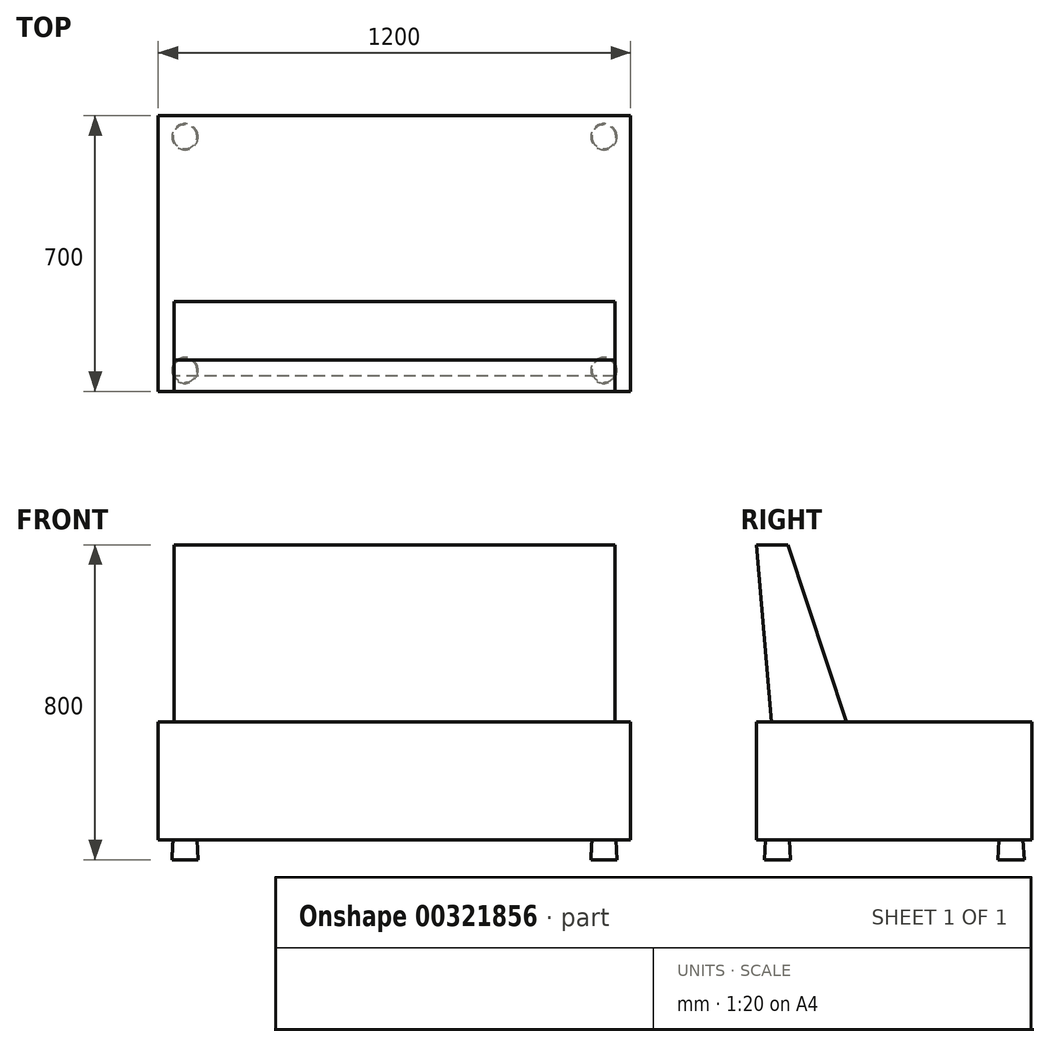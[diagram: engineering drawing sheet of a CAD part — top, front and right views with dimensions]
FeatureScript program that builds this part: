
annotation { "Feature Type Name" : "Feature", "Feature Type Description" : "" }
export const myFeature = defineFeature(function(context is Context, id is Id, definition is map)
    precondition{}
    {
        {
            var Q0;
            Q0=qCreatedBy(makeId("Top.planeOp"),FACE);
            var sketch = newSketch(context, id + "F0", { "sketchPlane" : qUnion([Q0])});
            skLineSegment(sketch, "E0.bottom", {"start": v(600, -350) * mm, "end": v(-600, -350) * mm});
            skLineSegment(sketch, "E0.top", {"start": v(600, 350) * mm, "end": v(-600, 350) * mm});
            skLineSegment(sketch, "E0.left", {"start": v(600, -350) * mm, "end": v(600, 350) * mm});
            skLineSegment(sketch, "E0.right", {"start": v(-600, -350) * mm, "end": v(-600, 350) * mm});
            skPoint(sketch, "E0.middle", {"position": v(0, 0) * mm});
            skSolve(sketch);
        }
        {
            var Q0;
            Q0=makeQuery(id+"F0.imprint","IMPRINT",FACE,{"disambiguationData":[TD([[makeQuery(id+"F0.imprint","IMPRINT",EDGE,{"derivedFrom":sQuery(id+"F0.wireOp",EDGE,"E0.bottom")}),-1.0]])]});
            extrude(context, id + "F1", {"entities" : qUnion([Q0]), "depth" : 300 * mm});
        }
        {
            var Q0;
            Q0=makeQuery(id+"F1.opExtrude","CAP_FACE",FACE,{"disambiguationData":[OSD([sQuery(id+"F0.wireOp",EDGE,"E0.bottom"),sQuery(id+"F0.wireOp",EDGE,"E0.top"),sQuery(id+"F0.wireOp",EDGE,"E0.left"),sQuery(id+"F0.wireOp",EDGE,"E0.right")])],"isStart":true});
            var sketch = newSketch(context, id + "F2", { "sketchPlane" : qUnion([Q0])});
            skLineSegment(sketch, "E1", {"start": v(-600, 0) * mm, "end": v(600, 0) * mm, "construction": true});
            skLineSegment(sketch, "E2", {"start": v(0, -350) * mm, "end": v(0, 350) * mm, "construction": true});
            skCircle(sketch, "E3", {"center": v(-532.1, -296.66) * mm, "radius": 30.5 * mm});
            skCircle(sketch, "E4.MirrorC", {"center": v(532.1, -296.66) * mm, "radius": 30.5 * mm});
            skCircle(sketch, "E5.MirrorC", {"center": v(532.1, 296.66) * mm, "radius": 30.5 * mm});
            skCircle(sketch, "E6.MirrorC", {"center": v(-532.1, 296.66) * mm, "radius": 30.5 * mm});
            skSolve(sketch);
        }
        {
            var Q0;
            Q0 = qSketchRegion(id + "F2", true);
            extrude(context, id + "F3", {"entities" : qUnion([Q0]), "operationType" : NewBodyOperationType.ADD, "depth" : 50 * mm, "hasDraft" : true, "draftAngle" : 3 * degree});
        }
        {
            var Q0;
            Q0=qCreatedBy(makeId("Right.planeOp"),FACE);
            var sketch = newSketch(context, id + "F4", { "sketchPlane" : qUnion([Q0])});
            skLineSegment(sketch, "E7", {"start": v(-107, 254.91) * mm, "end": v(-270.1, 750) * mm});
            skLineSegment(sketch, "E8", {"start": v(-270.1, 750) * mm, "end": v(-350, 750) * mm});
            skLineSegment(sketch, "E9", {"start": v(-350, 750) * mm, "end": v(-305.83, 230.6) * mm});
            skLineSegment(sketch, "E10", {"start": v(-305.83, 230.6) * mm, "end": v(-107, 254.91) * mm});
            skSolve(sketch);
        }
        {
            var Q0;
            Q0 = qSketchRegion(id + "F4", true);
            extrude(context, id + "F5", {"entities" : qUnion([Q0]), "operationType" : NewBodyOperationType.ADD, "endBound" : BoundingType.SYMMETRIC, "depth" : 1120 * mm});
        }
    });
